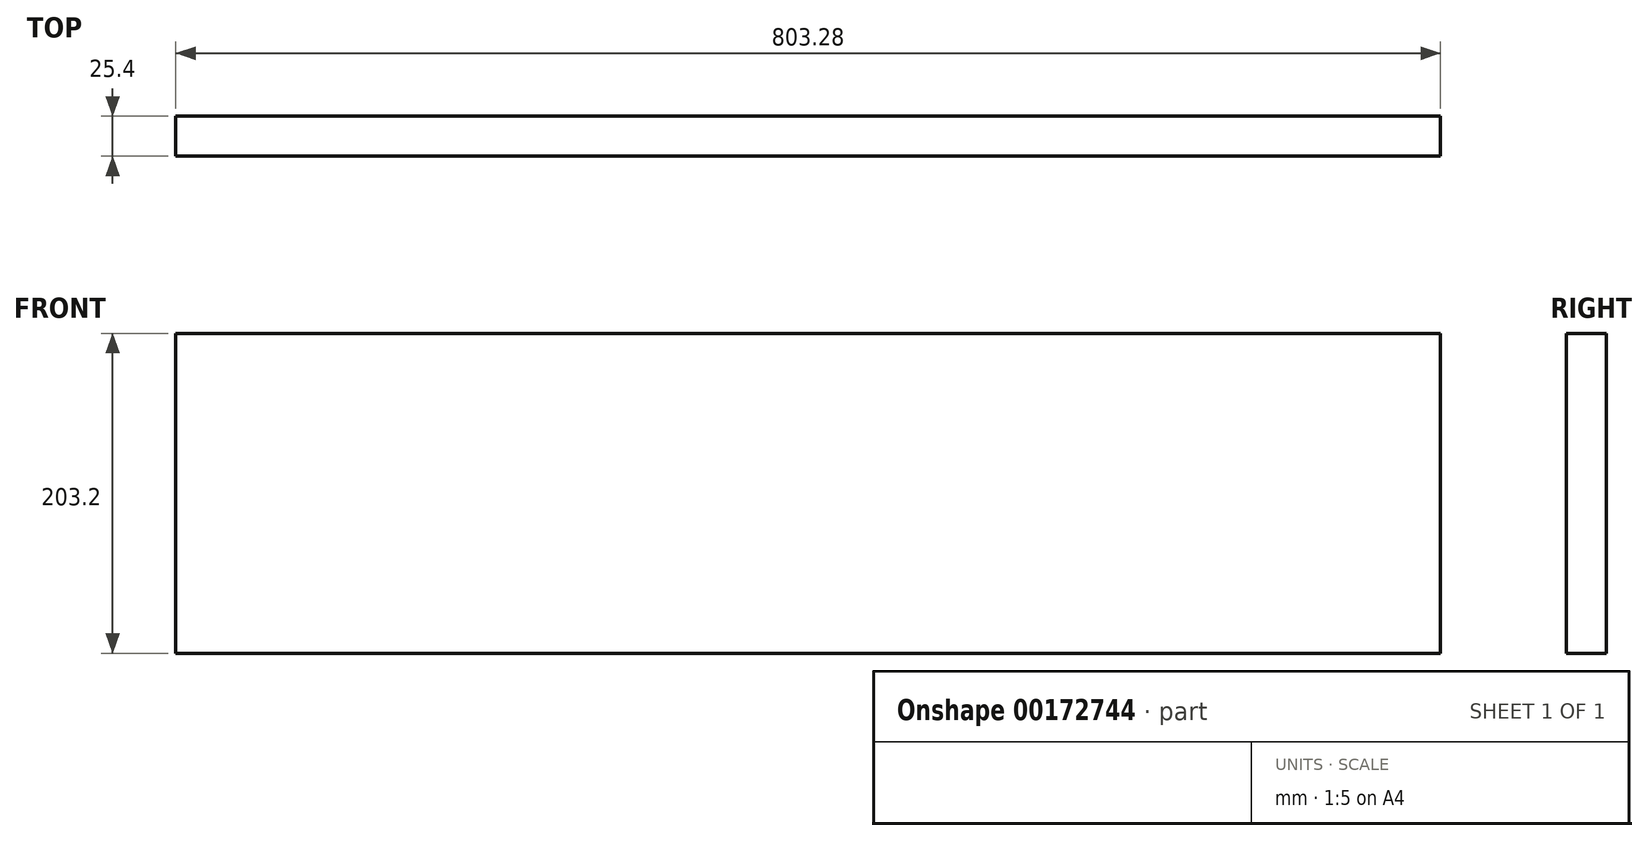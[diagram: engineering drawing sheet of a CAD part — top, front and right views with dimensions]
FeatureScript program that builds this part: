
annotation { "Feature Type Name" : "Feature", "Feature Type Description" : "" }
export const myFeature = defineFeature(function(context is Context, id is Id, definition is map)
    precondition{}
    {
        {
            var Q0;
            Q0=qCreatedBy(makeId("Front.planeOp"),FACE);
            var sketch = newSketch(context, id + "F0", { "sketchPlane" : qUnion([Q0])});
            skLineSegment(sketch, "E0.bottom", {"start": v(-411.08, -26.28) * mm, "end": v(392.2, -26.28) * mm});
            skLineSegment(sketch, "E0.top", {"start": v(-411.08, -229.48) * mm, "end": v(392.2, -229.48) * mm});
            skLineSegment(sketch, "E0.left", {"start": v(-411.08, -26.28) * mm, "end": v(-411.08, -229.48) * mm});
            skLineSegment(sketch, "E0.right", {"start": v(392.2, -26.28) * mm, "end": v(392.2, -229.48) * mm});
            skSolve(sketch);
        }
        {
            var Q0;
            Q0 = qSketchRegion(id + "F0", true);
            extrude(context, id + "F1", {"entities" : qUnion([Q0]), "depth" : 25.4 * mm});
        }
    });
